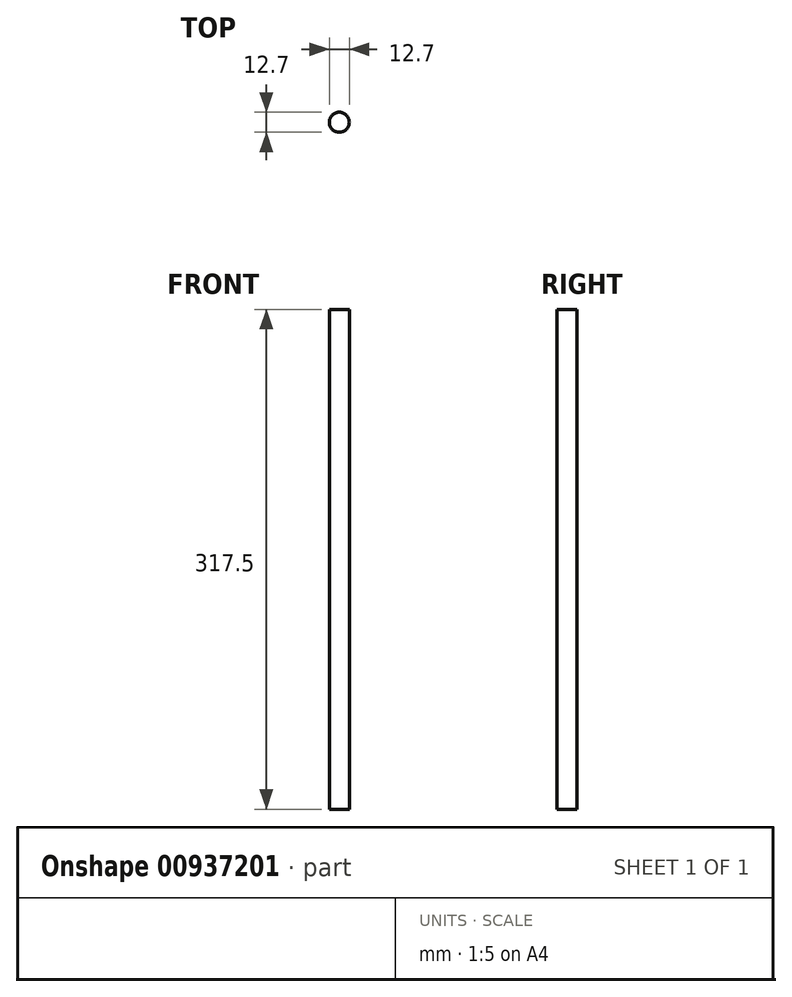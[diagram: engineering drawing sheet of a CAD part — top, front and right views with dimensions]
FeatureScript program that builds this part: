
annotation { "Feature Type Name" : "Feature", "Feature Type Description" : "" }
export const myFeature = defineFeature(function(context is Context, id is Id, definition is map)
    precondition{}
    {
        {
            var Q0;
            Q0=qCreatedBy(makeId("Top.planeOp"),FACE);
            var sketch = newSketch(context, id + "F0", { "sketchPlane" : qUnion([Q0])});
            skCircle(sketch, "E0", {"center": v(0, 0) * mm, "radius": 6.35 * mm});
            skSolve(sketch);
        }
        {
            var Q0;
            Q0 = qSketchRegion(id + "F0", true);
            extrude(context, id + "F1", {"entities" : qUnion([Q0]), "depth" : 317.5 * mm, "offsetDistance" : 25.4 * mm});
        }
    });
